# Revit family: AFX-Montclair_Pendant
name_source: partatom
category: Lighting Fixtures
units: mm (PartAtom-declared; Revit-internal decimal feet)

## family parameters
Cut with Voids When Loaded = No
Host = Face
Light Source = Yes
Part Type = Normal
Room Calculation Point = No
Round Connector Dimension = Use Diameter
Shared = No

## types (5) — shared parameters
Apparent Load = 0 VA
Assembly Code = D5020200
Color Filter = 16777215
Colour Rendering Index = 80
Cord Finish = AFX - Black Steel
Default Elevation = 48"
Diffuser Finish = AFX - White Acrylic
Dimming Lamp Color Temperature Shift = <None>
Emit Shape Visible in Rendering = No
Housing Finish = AFX - Black Steel
Keynote = 12500
Manufacturer = AFX Inc
Photometric Web File = MCP193200LxxD1SN-BK_IES.ies
Power Factor = 1
Product Documentation Link = https://www.afxinc.com
Revit File Built By = https://servex-us.com
Screen Finish = AFX - Fabric
Support Finish = AFX - Black Steel
Sustainability = https://lamprecycle.org
Tilt Angle = 90.00°
Type Comments = Montclair
URL = https://www.afxinc.com
Voltage = 120 V
Wattage Comments = 9

## per-type parameters (varying)
| type | Description | Diameter | Emit from Circle Diameter | Height |
| MCP1214LAJUDSN-BK | Pendant - 12 1/4"Dia x 3 3/4"H | 12 1/4" | 12" | 3 3/4" |
| MCP1524LAJUDSN-BK | Pendant - 15"Dia x 4 3/4"H | 15" | 15" | 4 3/4" |
| MCP1932LAJUDSN-BK | Pendant - 19 1/4"Dia x 5 1/2"H | 19 1/4" | 19" | 5 1/2" |
| MCP2432L5AJUDSN-BK | Pendant - 24"Dia x 7 1/2"H | 24" | 24" | 7 1/2" |
| MCP3044L5AJUDSN-BK | Pendant - 30"Dia x 9 1/2"H | 30" | 30" | 9 1/2" |

note: column(s) folded — value = type name in every type: Model

## geometry (parser evidence)
native form markers: Extrusion x1, Sweep x2
no freeform markers — native parametric forms only
